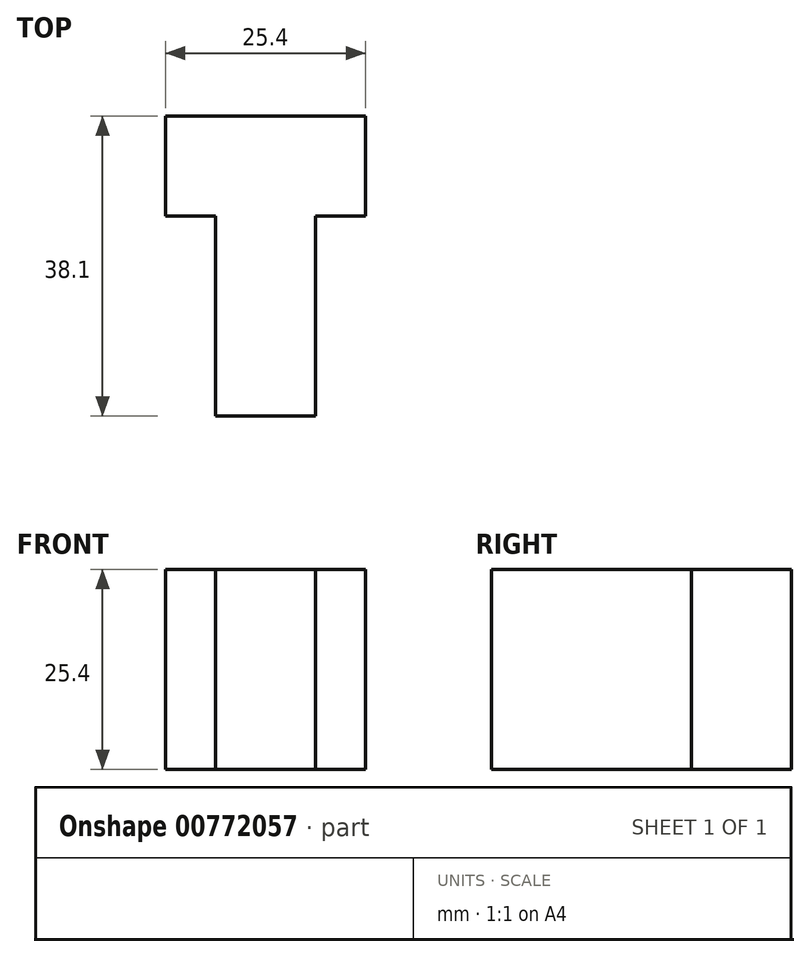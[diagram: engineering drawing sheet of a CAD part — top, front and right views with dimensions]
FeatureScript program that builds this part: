
annotation { "Feature Type Name" : "Feature", "Feature Type Description" : "" }
export const myFeature = defineFeature(function(context is Context, id is Id, definition is map)
    precondition{}
    {
        {
            var Q0;
            Q0=qCreatedBy(makeId("Top.planeOp"),FACE);
            var sketch = newSketch(context, id + "F0", { "sketchPlane" : qUnion([Q0])});
            skLineSegment(sketch, "E0", {"start": v(0, 0) * mm, "end": v(0, -25.4) * mm});
            skLineSegment(sketch, "E1", {"start": v(0, -25.4) * mm, "end": v(12.7, -25.4) * mm});
            skLineSegment(sketch, "E2", {"start": v(12.7, -25.4) * mm, "end": v(12.7, 0) * mm});
            skLineSegment(sketch, "E3", {"start": v(12.7, 0) * mm, "end": v(19.05, 0) * mm});
            skLineSegment(sketch, "E4", {"start": v(0, 0) * mm, "end": v(-6.35, 0) * mm});
            skLineSegment(sketch, "E5", {"start": v(-6.35, 0) * mm, "end": v(-6.35, 12.7) * mm});
            skLineSegment(sketch, "E6", {"start": v(19.05, 0) * mm, "end": v(19.05, 12.7) * mm});
            skLineSegment(sketch, "E7", {"start": v(-6.35, 12.7) * mm, "end": v(19.05, 12.7) * mm});
            skSolve(sketch);
        }
        {
            var Q0;
            Q0=makeQuery(id+"F0.imprint","IMPRINT",FACE,{"disambiguationData":[TD([[makeQuery(id+"F0.imprint","IMPRINT",EDGE,{"derivedFrom":sQuery(id+"F0.wireOp",EDGE,"E0")}),1.0]])]});
            extrude(context, id + "F1", {"entities" : qUnion([Q0]), "depth" : 25.4 * mm, "offsetDistance" : 25.4 * mm});
        }
    });
